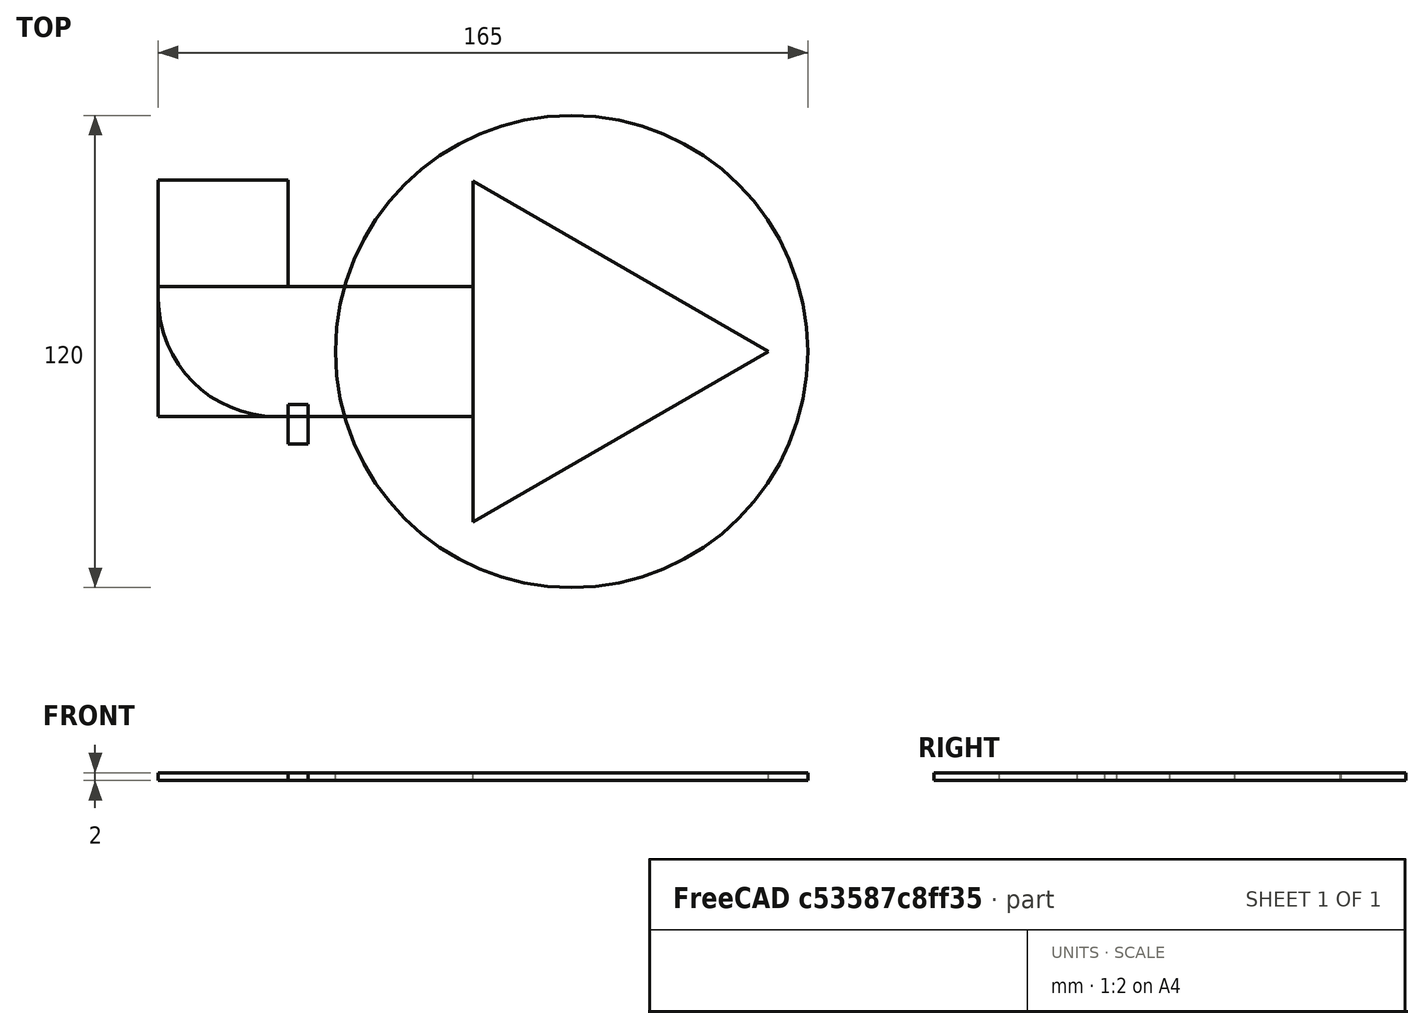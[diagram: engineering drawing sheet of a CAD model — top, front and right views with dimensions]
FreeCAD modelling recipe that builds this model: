
FCSTD DOCUMENT  (FreeCAD 0.19R24291 (Git))
Label: Frechas
License: All rights reserved
LicenseURL: http://en.wikipedia.org/wiki/All_rights_reserved
objects: Part::Box×4, Part::Extrusion×2, Part::RegularPolygon×1, Part::MultiFuse×1, Part::Fillet×1, Part::Cylinder×1
note: 10 computed .brp shape members not serialized (recipe doc carries the construction recipe); baked Part::Feature solids carry a one-line shape summary decoded from their .brp

FEATURE [Part::Box] Box  label="Rabo"
  AttacherType = Attacher::AttachEngine3D
  Height = 2
  Length = 80
  Placement = pos=(-105,-16.5,0) rot=(0,0,1;0rad)
  Width = 33
FEATURE [Part::RegularPolygon] RegularPolygon002  label="Polígono regular002"
  AttacherType = Attacher::AttachEngine3D
  Circumradius = 50
  Polygon = 3
FEATURE [Part::Extrusion] Extrude
  Base = -> RegularPolygon002
  Dir = (0,0,2)
  DirMode = 0
  FaceMakerClass = Part::FaceMakerExtrusion
  LengthFwd = 0
  LengthRev = 0
  Solid = true
  Symmetric = false
FEATURE [Part::Extrusion] Extrude001  label="Frecha"
  Base = -> RegularPolygon002
  Dir = (0,0,2)
  DirMode = 0
  FaceMakerClass = Part::FaceMakerExtrusion
  LengthFwd = 0
  LengthRev = 0
  Solid = true
  Symmetric = false
FEATURE [Part::Box] Box001  label="Cubo001"
  AttacherType = Attacher::AttachEngine3D
  Height = 2
  Length = 60
  Placement = pos=(-72,-16.5,0) rot=(0,0,1;1.5708rad)
  Width = 33
FEATURE [Part::Box] Box002  label="Cubo002"
  AttacherType = Attacher::AttachEngine3D
  Height = 2
  Length = 80
  Placement = pos=(-105,-16.5,0) rot=(0,0,1;0rad)
  Width = 33
FEATURE [Part::MultiFuse] Fusion
  Shapes = -> [Box002,Box001]
FEATURE [Part::Fillet] Fillet  label="Xiro"
  Base = -> Fusion
  Edges = 1 edges r=30: [Edge14]
FEATURE [Part::Cylinder] Cylinder  label="circulo"
  Angle = 360
  AttacherType = Attacher::AttachEngine3D
  Height = 2
  Radius = 60
FEATURE [Part::Box] Box003  label="cubo"
  AttacherType = Attacher::AttachEngine3D
  Height = 2
  Length = 5
  Placement = pos=(-72,-23.5,0) rot=(0,0,1;0rad)
  Width = 10
